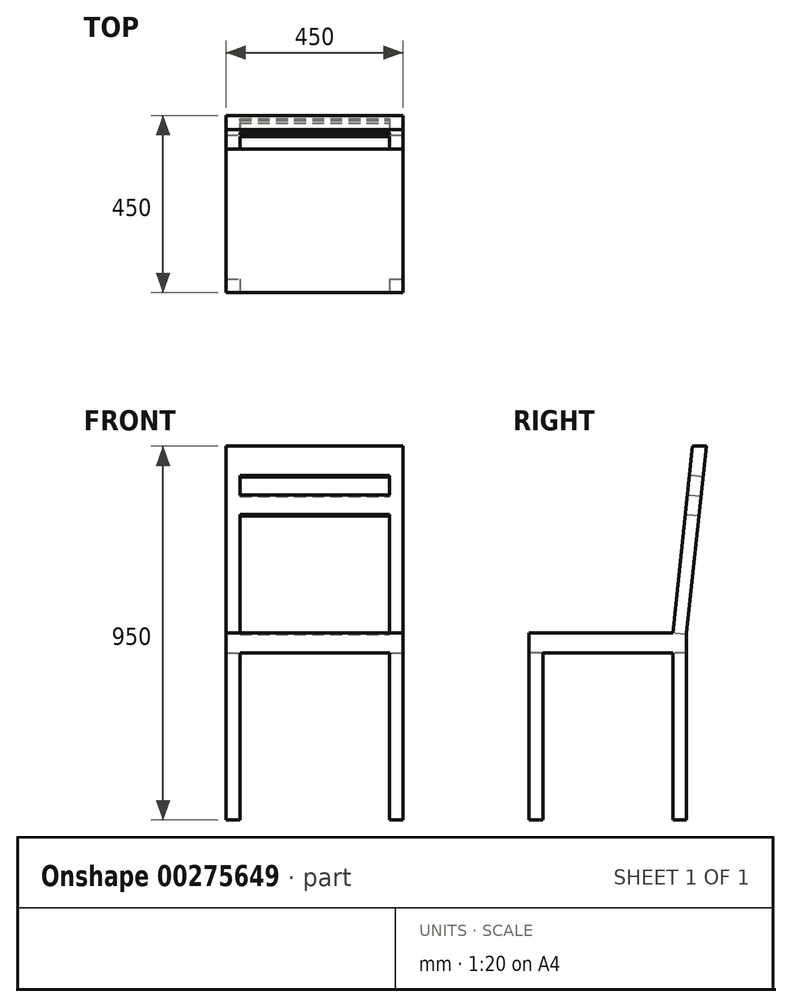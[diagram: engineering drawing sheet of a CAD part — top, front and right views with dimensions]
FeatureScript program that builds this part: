
annotation { "Feature Type Name" : "Feature", "Feature Type Description" : "" }
export const myFeature = defineFeature(function(context is Context, id is Id, definition is map)
    precondition{}
    {
        {
            var Q0;
            Q0=qCreatedBy(makeId("Top.planeOp"),FACE);
            var sketch = newSketch(context, id + "F0", { "sketchPlane" : qUnion([Q0])});
            skLineSegment(sketch, "E0.bottom", {"start": v(225, 225) * mm, "end": v(-225, 225) * mm});
            skLineSegment(sketch, "E0.top", {"start": v(225, -225) * mm, "end": v(-225, -225) * mm});
            skLineSegment(sketch, "E0.left", {"start": v(225, 225) * mm, "end": v(225, -225) * mm});
            skLineSegment(sketch, "E0.right", {"start": v(-225, 225) * mm, "end": v(-225, -225) * mm});
            skPoint(sketch, "E0.middle", {"position": v(0, 0) * mm});
            skSolve(sketch);
        }
        {
            var Q0;
            Q0=qSketchRegion(id+"F0",true);
            extrude(context, id + "F1", {"entities" : qUnion([Q0]), "depth" : 950 * mm});
        }
        {
            var Q0;
            Q0=makeQuery(id+"F1.opExtrude","SWEPT_FACE",FACE,{"disambiguationData":[OSD([sQuery(id+"F0.wireOp",EDGE,"E0.left")])]});
            var sketch = newSketch(context, id + "F2", { "sketchPlane" : qUnion([Q0])});
            skLineSegment(sketch, "E1.bottom", {"start": v(-225, 475) * mm, "end": v(225, 475) * mm});
            skLineSegment(sketch, "E1.top", {"start": v(-225, 425) * mm, "end": v(225, 425) * mm});
            skLineSegment(sketch, "E1.left", {"start": v(-225, 475) * mm, "end": v(-225, 425) * mm});
            skLineSegment(sketch, "E1.right", {"start": v(225, 475) * mm, "end": v(225, 425) * mm});
            skLineSegment(sketch, "E2", {"start": v(225, 950) * mm, "end": v(175, 475) * mm});
            skLineSegment(sketch, "E3", {"start": v(189.8, 950) * mm, "end": v(139.8, 475) * mm});
            skLineSegment(sketch, "E4", {"start": v(175, 475) * mm, "end": v(175, 0) * mm});
            skLineSegment(sketch, "E5", {"start": v(139.8, 475) * mm, "end": v(139.8, 0) * mm});
            skLineSegment(sketch, "E6", {"start": v(-225, 425) * mm, "end": v(-225, 0) * mm});
            skLineSegment(sketch, "E7", {"start": v(-190, 425) * mm, "end": v(-190, -18.95) * mm});
            skSolve(sketch);
        }
        {
            var Q0;
            {var subQ0=sQuery(id+"F2.wireOp",EDGE,"E1.right");Q0=makeQuery(id+"F2.imprint","IMPRINT",FACE,{"disambiguationData":[TD([[makeQuery(id+"F2.imprint","IMPRINT",EDGE,{"derivedFrom":subQ0}),-1.0]])]});}
            var Q1;
            {var subQ4=sQuery(id+"F2.wireOp",EDGE,"E3");Q1=makeQuery(id+"F2.imprint","IMPRINT",FACE,{"disambiguationData":[TD([[makeQuery(id+"F2.imprint","IMPRINT",EDGE,{"derivedFrom":subQ4}),-1.0]])]});}
            var Q2;
            {var subQ4=sQuery(id+"F2.wireOp",EDGE,"E2");Q2=makeQuery(id+"F2.imprint","IMPRINT",FACE,{"disambiguationData":[TD([[makeQuery(id+"F2.imprint","IMPRINT",EDGE,{"derivedFrom":subQ4}),1.0]])]});}
            var Q3;
            {var subQ0=sQuery(id+"F2.wireOp",EDGE,"E7");var subQ1=sQuery(id+"F2.wireOp",EDGE,"E1.top");var subQ2=makeQuery(id+"F2.imprint","INTERSECT",VERTEX,{"derivedFrom":[subQ1,subQ0]});Q3=makeQuery(id+"F2.imprint","IMPRINT",FACE,{"disambiguationData":[TD([[makeQuery(id+"F2.imprint","IMPRINT",EDGE,{"disambiguationData":[TD([[subQ2,-1.0]])],"derivedFrom":subQ1}),-1.0]])]});}
            var Q4;
            {var subQ1=sQuery(id+"F0.wireOp",EDGE,"E0.left");var subQ4=sQuery(id+"F2.wireOp",EDGE,"E4");var subQ6=makeQuery(id+"F1.opExtrude","CAP_EDGE",EDGE,{"disambiguationData":[OSD([subQ1])],"isStart":true});var subQ7=makeQuery(id+"F2.imprint","INTERSECT",VERTEX,{"derivedFrom":[subQ6,subQ4]});Q4=makeQuery(id+"F2.imprint","IMPRINT",FACE,{"disambiguationData":[TD([[makeQuery(id+"F2.imprint","IMPRINT",EDGE,{"disambiguationData":[TD([[subQ7,1.0]])],"derivedFrom":subQ4}),1.0]])]});}
            extrude(context, id + "F3", {"entities" : qUnion([Q0, Q1, Q2, Q3, Q4]), "operationType" : NewBodyOperationType.REMOVE, "endBound" : BoundingType.THROUGH_ALL, "oppositeDirection" : true, "depth" : 25 * mm});
        }
        {
            var Q0;
            Q0=makeQuery(id+"F1.opExtrude","SWEPT_FACE",FACE,{"disambiguationData":[OSD([sQuery(id+"F0.wireOp",EDGE,"E0.top")])]});
            var sketch = newSketch(context, id + "F4", { "sketchPlane" : qUnion([Q0])});
            skLineSegment(sketch, "E8", {"start": v(-190, 0) * mm, "end": v(-190, 425) * mm});
            skLineSegment(sketch, "E9", {"start": v(-190, 425) * mm, "end": v(190, 425) * mm});
            skLineSegment(sketch, "E10", {"start": v(190, 425) * mm, "end": v(190, 0) * mm});
            skSolve(sketch);
        }
        {
            var Q0;
            Q0 = qSketchRegion(id + "F4", true);
            var Q1;
            {var subQ0=sQuery(id+"F4.wireOp",EDGE,"E8");Q1=makeQuery(id+"F4.imprint","IMPRINT",FACE,{"disambiguationData":[TD([[makeQuery(id+"F4.imprint","IMPRINT",EDGE,{"derivedFrom":subQ0}),-1.0]])]});}
            extrude(context, id + "F5", {"entities" : qUnion([Q0, Q1]), "operationType" : NewBodyOperationType.REMOVE, "endBound" : BoundingType.THROUGH_ALL, "oppositeDirection" : true, "depth" : 25 * mm});
        }
        {
            var Q0;
            Q0=makeQuery(id+"F3.boolean.opBoolean","COPY",FACE,{"derivedFrom":makeQuery(id+"F3.opExtrude","SWEPT_FACE",FACE,{"disambiguationData":[OSD([sQuery(id+"F2.wireOp",EDGE,"E3")])]})});
            var sketch = newSketch(context, id + "F6", { "sketchPlane" : qUnion([Q0])});
            skLineSegment(sketch, "E11", {"start": v(-190, 487.03) * mm, "end": v(-190, 889.65) * mm});
            skLineSegment(sketch, "E12", {"start": v(-190, 889.65) * mm, "end": v(190, 889.65) * mm});
            skLineSegment(sketch, "E13", {"start": v(190, 889.65) * mm, "end": v(190, 487.03) * mm});
            skLineSegment(sketch, "E14", {"start": v(-190, 839.65) * mm, "end": v(190, 839.65) * mm});
            skLineSegment(sketch, "E15", {"start": v(-190, 789.65) * mm, "end": v(190, 789.65) * mm});
            skPoint(sketch, "E15.startSnap0", {"position": v(-227.7, 789.65) * mm});
            skSolve(sketch);
        }
        {
            var Q0;
            {var subQ3=sQuery(id+"F6.wireOp",EDGE,"E15");Q0=makeQuery(id+"F6.imprint","IMPRINT",FACE,{"disambiguationData":[TD([[makeQuery(id+"F6.imprint","IMPRINT",EDGE,{"derivedFrom":subQ3}),-1.0]])]});}
            var Q1;
            {var subQ0=sQuery(id+"F6.wireOp",EDGE,"E12");Q1=makeQuery(id+"F6.imprint","IMPRINT",FACE,{"disambiguationData":[TD([[makeQuery(id+"F6.imprint","IMPRINT",EDGE,{"derivedFrom":subQ0}),-1.0]])]});}
            extrude(context, id + "F7", {"entities" : qUnion([Q0, Q1]), "operationType" : NewBodyOperationType.REMOVE, "endBound" : BoundingType.THROUGH_ALL, "oppositeDirection" : true, "depth" : 25 * mm});
        }
    });
